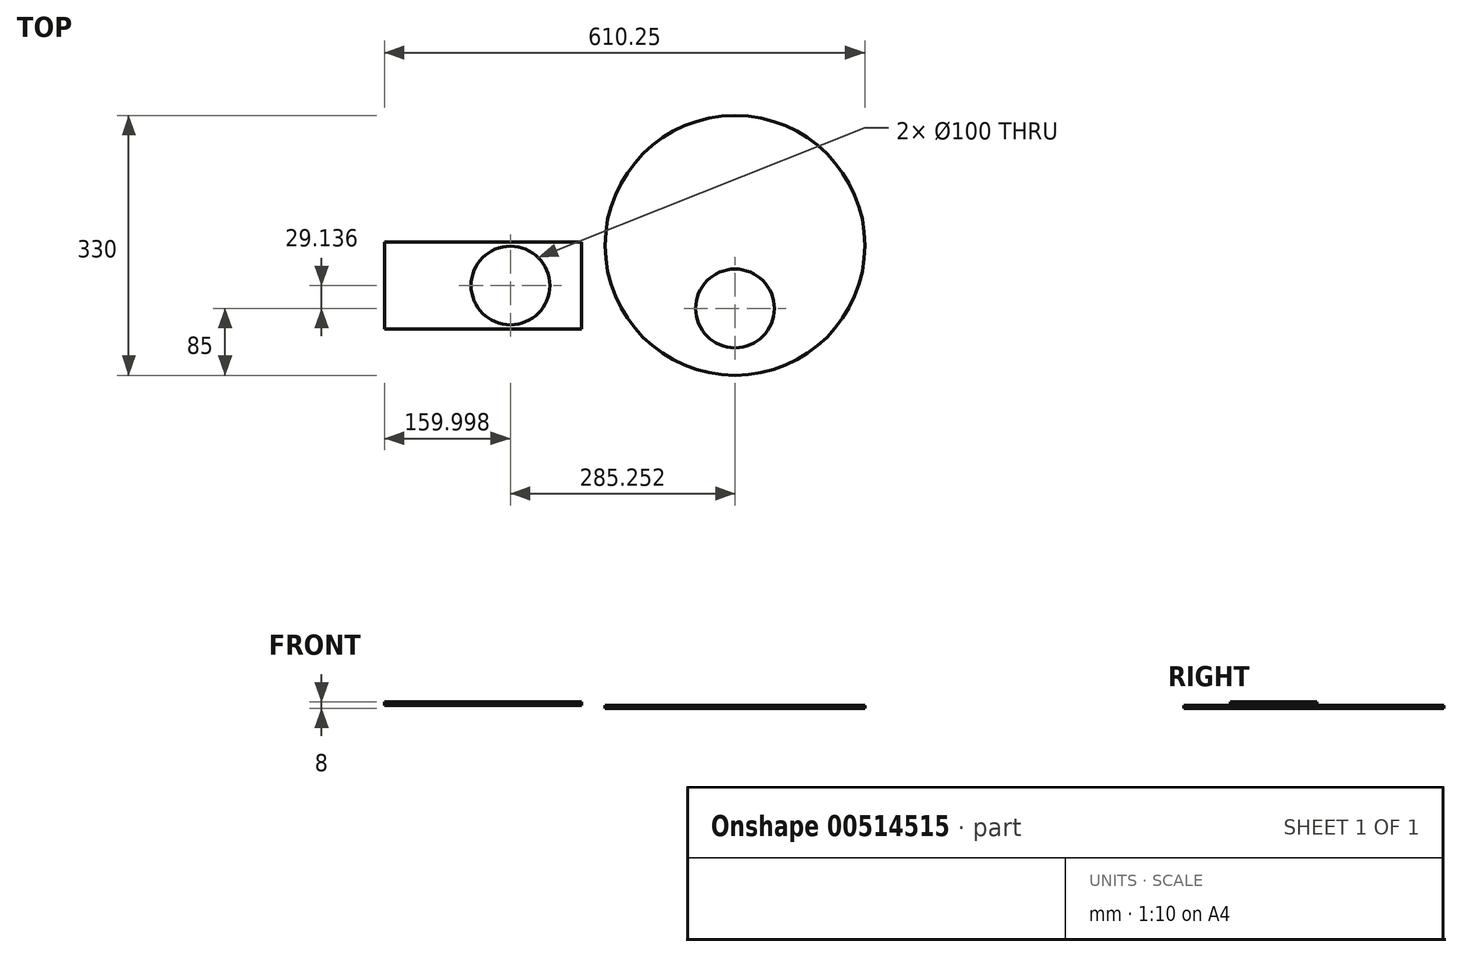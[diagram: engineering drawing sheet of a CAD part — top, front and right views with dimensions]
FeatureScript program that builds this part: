
annotation { "Feature Type Name" : "Feature", "Feature Type Description" : "" }
export const myFeature = defineFeature(function(context is Context, id is Id, definition is map)
    precondition{}
    {
        {
            var Q0;
            Q0=qCreatedBy(makeId("Top.planeOp"),FACE);
            var sketch = newSketch(context, id + "F0", { "sketchPlane" : qUnion([Q0])});
            skCircle(sketch, "E0", {"center": v(0, 0) * mm, "radius": 165 * mm});
            skCircle(sketch, "E1", {"center": v(0, -80) * mm, "radius": 50 * mm});
            skCircle(sketch, "E2", {"center": v(0, 0) * mm, "radius": 155 * mm, "construction": true});
            skSolve(sketch);
        }
        {
            var Q0;
            Q0=makeQuery(id+"F0.imprint","IMPRINT",FACE,{"disambiguationData":[TD([[makeQuery(id+"F0.imprint","IMPRINT",EDGE,{"derivedFrom":sQuery(id+"F0.wireOp",EDGE,"E0")}),1.0]])]});
            extrude(context, id + "F1", {"entities" : qUnion([Q0]), "depth" : 4 * mm});
        }
        {
            var Q0;
            Q0=makeQuery(id+"F1.opExtrude","CAP_FACE",FACE,{"disambiguationData":[OSD([sQuery(id+"F0.wireOp",EDGE,"E0"),sQuery(id+"F0.wireOp",EDGE,"E1")])],"isStart":false});
            var sketch = newSketch(context, id + "F2", { "sketchPlane" : qUnion([Q0])});
            skCircle(sketch, "E3", {"center": v(-285.25, -50.86) * mm, "radius": 50 * mm});
            skLineSegment(sketch, "E4.bottom", {"start": v(-445.25, 4.14) * mm, "end": v(-195.25, 4.14) * mm});
            skLineSegment(sketch, "E4.top", {"start": v(-445.25, -105.86) * mm, "end": v(-195.25, -105.86) * mm});
            skLineSegment(sketch, "E4.left", {"start": v(-445.25, 4.14) * mm, "end": v(-445.25, -105.86) * mm});
            skLineSegment(sketch, "E4.right", {"start": v(-195.25, 4.14) * mm, "end": v(-195.25, -105.86) * mm});
            skPoint(sketch, "E5", {"position": v(-445.25, -50.86) * mm});
            skPoint(sketch, "E6", {"position": v(-195.25, -50.86) * mm});
            skLineSegment(sketch, "E7", {"start": v(-445.25, -50.86) * mm, "end": v(-195.25, -50.86) * mm, "construction": true});
            skSolve(sketch);
        }
        {
            var Q0;
            Q0 = qSketchRegion(id + "F2", true);
            extrude(context, id + "F3", {"entities" : qUnion([Q0]), "depth" : 4 * mm});
        }
    });
